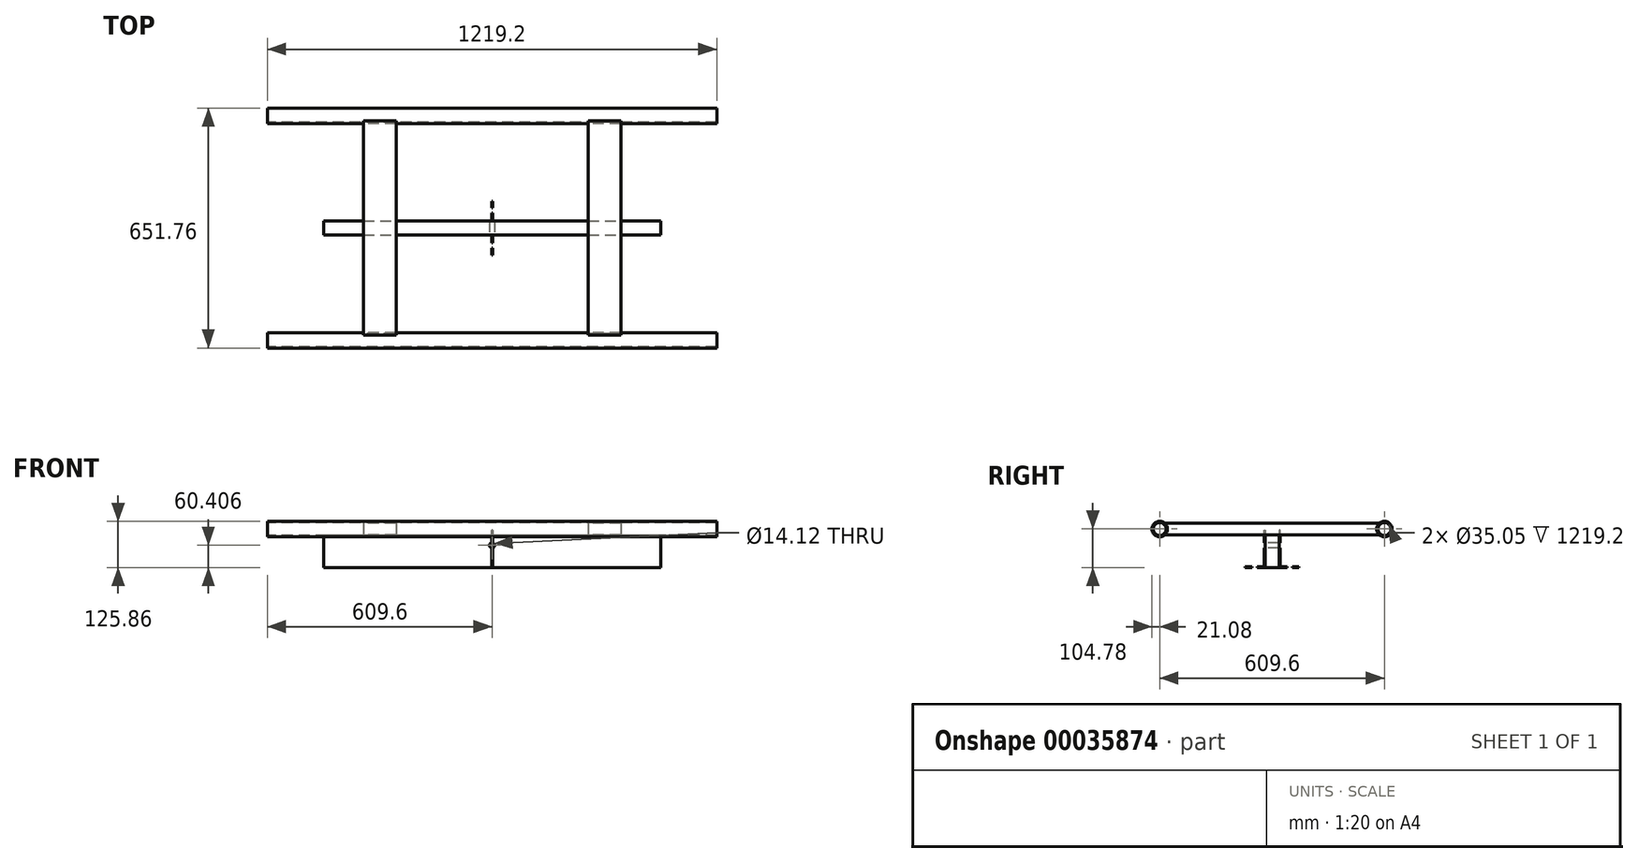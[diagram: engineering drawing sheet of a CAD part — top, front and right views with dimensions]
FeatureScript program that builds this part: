
annotation { "Feature Type Name" : "Feature", "Feature Type Description" : "" }
export const myFeature = defineFeature(function(context is Context, id is Id, definition is map)
    precondition{}
    {
        {
            var Q0;
            Q0=qCreatedBy(makeId("Right.planeOp"),FACE);
            var sketch = newSketch(context, id + "F0", { "sketchPlane" : qUnion([Q0])});
            skCircle(sketch, "E0", {"center": v(-304.8, 0) * mm, "radius": 21.08 * mm});
            skCircle(sketch, "E1", {"center": v(304.8, 0) * mm, "radius": 21.08 * mm});
            skLineSegment(sketch, "E2", {"start": v(-283.72, 0) * mm, "end": v(283.72, 0) * mm, "construction": true});
            skCircle(sketch, "E3", {"center": v(-304.8, 0) * mm, "radius": 17.53 * mm});
            skCircle(sketch, "E4", {"center": v(304.8, 0) * mm, "radius": 17.53 * mm});
            skPoint(sketch, "E5.rect.middle", {"position": v(0, 0) * mm});
            skSolve(sketch);
        }
        {
            var Q0;
            Q0=makeQuery(id+"F0.imprint","IMPRINT",FACE,{"disambiguationData":[TD([[makeQuery(id+"F0.imprint","IMPRINT",EDGE,{"derivedFrom":sQuery(id+"F0.wireOp",EDGE,"E0")}),1.0]])]});
            var Q1;
            Q1=makeQuery(id+"F0.imprint","IMPRINT",FACE,{"disambiguationData":[TD([[makeQuery(id+"F0.imprint","IMPRINT",EDGE,{"derivedFrom":sQuery(id+"F0.wireOp",EDGE,"E1")}),1.0]])]});
            extrude(context, id + "F1", {"entities" : qUnion([Q0, Q1]), "endBound" : BoundingType.SYMMETRIC, "depth" : 1219.2 * mm});
        }
        {
            var Q0;
            Q0=qCreatedBy(makeId("Front.planeOp"),FACE);
            var sketch = newSketch(context, id + "F2", { "sketchPlane" : qUnion([Q0])});
            skLineSegment(sketch, "E6", {"start": v(-304.8, 0) * mm, "end": v(304.8, 0) * mm, "construction": true});
            skLineSegment(sketch, "E7.rect.bottom", {"start": v(-260.35, -15.87) * mm, "end": v(-349.25, -15.87) * mm});
            skLineSegment(sketch, "E7.rect.top", {"start": v(-260.35, 15.88) * mm, "end": v(-349.25, 15.88) * mm});
            skLineSegment(sketch, "E7.rect.left", {"start": v(-260.35, -15.87) * mm, "end": v(-260.35, 15.88) * mm});
            skLineSegment(sketch, "E7.rect.right", {"start": v(-349.25, -15.87) * mm, "end": v(-349.25, 15.88) * mm});
            skPoint(sketch, "E7.rect.middle", {"position": v(-304.8, 0) * mm});
            skLineSegment(sketch, "E8.rect.bottom", {"start": v(349.25, -15.87) * mm, "end": v(260.35, -15.88) * mm});
            skLineSegment(sketch, "E8.rect.top", {"start": v(349.25, 15.88) * mm, "end": v(260.35, 15.88) * mm});
            skLineSegment(sketch, "E8.rect.left", {"start": v(349.25, -15.87) * mm, "end": v(349.25, 15.88) * mm});
            skLineSegment(sketch, "E8.rect.right", {"start": v(260.35, -15.88) * mm, "end": v(260.35, 15.88) * mm});
            skPoint(sketch, "E8.rect.middle", {"position": v(304.8, 0) * mm});
            skSolve(sketch);
        }
        {
            var Q0;
            Q0=makeQuery(id+"F2.imprint","IMPRINT",FACE,{"disambiguationData":[TD([[makeQuery(id+"F2.imprint","IMPRINT",EDGE,{"derivedFrom":sQuery(id+"F2.wireOp",EDGE,"E7.rect.bottom")}),-1.0]])]});
            var Q1;
            Q1=makeQuery(id+"F2.imprint","IMPRINT",FACE,{"disambiguationData":[TD([[makeQuery(id+"F2.imprint","IMPRINT",EDGE,{"derivedFrom":sQuery(id+"F2.wireOp",EDGE,"E8.rect.bottom")}),-1.0]])]});
            extrude(context, id + "F3", {"entities" : qUnion([Q0, Q1]), "endBound" : BoundingType.UP_TO_NEXT, "depth" : 25.4 * mm, "hasSecondDirection" : true, "secondDirectionBound" : SecondDirectionBoundingType.UP_TO_NEXT, "secondDirectionOppositeDirection" : true, "secondDirectionDepth" : 25.4 * mm});
        }
        {
            assignVariable(context, id + "F4", {"name" : "bcLength", "anyValue" : 914.4 * mm});
        }
        {
            var Q0;
            Q0=qCreatedBy(makeId("Right.planeOp"),FACE);
            var sketch = newSketch(context, id + "F5", { "sketchPlane" : qUnion([Q0])});
            skLineSegment(sketch, "E9.bottom", {"start": v(-19.05, -15.88) * mm, "end": v(19.05, -15.88) * mm});
            skLineSegment(sketch, "E9.top", {"start": v(-19.05, -104.78) * mm, "end": v(19.05, -104.78) * mm});
            skLineSegment(sketch, "E9.left", {"start": v(-19.05, -104.78) * mm, "end": v(-19.05, -15.88) * mm});
            skLineSegment(sketch, "E9.right", {"start": v(19.05, -104.78) * mm, "end": v(19.05, -15.87) * mm});
            skPoint(sketch, "E10", {"position": v(0, -15.88) * mm});
            skPoint(sketch, "E11", {"position": v(0, -104.78) * mm});
            skLineSegment(sketch, "E12", {"start": v(0, -104.78) * mm, "end": v(0, -15.88) * mm, "construction": true});
            skSolve(sketch);
        }
        {
            var Q0;
            Q0 = qSketchRegion(id + "F5", true);
            extrude(context, id + "F6", {"entities" : qUnion([Q0]), "endBound" : BoundingType.SYMMETRIC, "oppositeDirection" : true, "depth" : getVariable(context, 'bcLength')});
        }
        {
            assignVariable(context, id + "F7", {"name" : "joistwidth", "anyValue" : 2.5});
        }
        {
            var Q0;
            Q0=qCreatedBy(makeId("Right.planeOp"),FACE);
            var sketch = newSketch(context, id + "F8", { "sketchPlane" : qUnion([Q0])});
            skLineSegment(sketch, "E13", {"start": v(19.05, -3.17) * mm, "end": v(19.05, -104.78) * mm});
            skLineSegment(sketch, "E14", {"start": v(19.05, -104.78) * mm, "end": v(73.03, -104.78) * mm});
            skLineSegment(sketch, "E15", {"start": v(73.03, -104.78) * mm, "end": v(73.03, -102.02) * mm});
            skLineSegment(sketch, "E16", {"start": v(73.03, -102.02) * mm, "end": v(21.8, -102.02) * mm});
            skLineSegment(sketch, "E17", {"start": v(21.8, -102.02) * mm, "end": v(21.8, -3.17) * mm});
            skLineSegment(sketch, "E18", {"start": v(21.8, -3.17) * mm, "end": v(19.05, -3.17) * mm});
            skLineSegment(sketch, "E19", {"start": v(0, 58.44) * mm, "end": v(0, -123.14) * mm, "construction": true});
            skLineSegment(sketch, "E20.MirrorCS", {"start": v(-21.8, -3.17) * mm, "end": v(-19.05, -3.17) * mm});
            skLineSegment(sketch, "E21.MirrorCS", {"start": v(-73.03, -104.78) * mm, "end": v(-73.03, -102.02) * mm});
            skLineSegment(sketch, "E22.MirrorCS", {"start": v(-19.05, -104.78) * mm, "end": v(-73.03, -104.78) * mm});
            skLineSegment(sketch, "E23.MirrorCS", {"start": v(-21.8, -102.02) * mm, "end": v(-21.8, -3.17) * mm});
            skLineSegment(sketch, "E24.MirrorCS", {"start": v(-73.03, -102.02) * mm, "end": v(-21.8, -102.02) * mm});
            skLineSegment(sketch, "E25.MirrorCS", {"start": v(-19.05, -3.17) * mm, "end": v(-19.05, -104.78) * mm});
            skSolve(sketch);
        }
        {
            assignVariable(context, id + "F9", {"name" : "joistwidth", "anyValue" : 2.5});
        }
        {
            var Q0;
            Q0 = qSketchRegion(id + "F8", true);
            extrude(context, id + "F10", {"entities" : qUnion([Q0]), "endBound" : BoundingType.SYMMETRIC, "depth" : (getVariable(context, 'joistwidth')) * mm});
        }
        {
            var Q0;
            Q0=makeQuery(id+"F10.opExtrude","SWEPT_EDGE",EDGE,{"disambiguationData":[OSD([sQuery(id+"F8.wireOp",EDGE,"E16"),sQuery(id+"F8.wireOp",EDGE,"E17")])]});
            var Q1;
            Q1=makeQuery(id+"F10.opExtrude","SWEPT_EDGE",EDGE,{"disambiguationData":[OSD([sQuery(id+"F8.wireOp",EDGE,"E13"),sQuery(id+"F8.wireOp",EDGE,"E14")])]});
            var Q2;
            Q2=makeQuery(id+"F10.opExtrude","SWEPT_EDGE",EDGE,{"disambiguationData":[OSD([sQuery(id+"F8.wireOp",EDGE,"E22.MirrorCS"),sQuery(id+"F8.wireOp",EDGE,"E25.MirrorCS")])]});
            var Q3;
            Q3=makeQuery(id+"F10.opExtrude","SWEPT_EDGE",EDGE,{"disambiguationData":[OSD([sQuery(id+"F8.wireOp",EDGE,"E23.MirrorCS"),sQuery(id+"F8.wireOp",EDGE,"E24.MirrorCS")])]});
            fillet(context, id + "F11", {"entities" : qUnion([Q0, Q1, Q2, Q3]), "radius" : 2.54 * mm, "tangentPropagation" : true, "allowEdgeOverflow" : false});
        }
        {
            var Q0;
            Q0=qCreatedBy(makeId("Front.planeOp"),FACE);
            var sketch = newSketch(context, id + "F12", { "sketchPlane" : qUnion([Q0])});
            skCircle(sketch, "E26", {"center": v(0, -44.37) * mm, "radius": 7.06 * mm});
            skSolve(sketch);
        }
        {
            var Q0;
            Q0 = qSketchRegion(id + "F12", true);
            extrude(context, id + "F13", {"entities" : qUnion([Q0]), "operationType" : NewBodyOperationType.REMOVE, "endBound" : BoundingType.SYMMETRIC, "oppositeDirection" : true, "depth" : 101.6 * mm, "hasSecondDirection" : true, "secondDirectionOppositeDirection" : false, "secondDirectionDepth" : 25.4 * mm});
        }
        {
            var Q0;
            Q0=makeQuery(id+"F10.opExtrude","SWEPT_FACE",FACE,{"disambiguationData":[OSD([sQuery(id+"F8.wireOp",EDGE,"E24.MirrorCS")])]});
            var sketch = newSketch(context, id + "F14", { "sketchPlane" : qUnion([Q0])});
            skCircle(sketch, "E27", {"center": v(0, -47.62) * mm, "radius": 7.06 * mm});
            skCircle(sketch, "E28.MirrorC", {"center": v(0, 47.63) * mm, "radius": 7.06 * mm});
            skSolve(sketch);
        }
        {
            var Q0;
            Q0 = qSketchRegion(id + "F14", true);
            extrude(context, id + "F15", {"entities" : qUnion([Q0]), "operationType" : NewBodyOperationType.REMOVE, "endBound" : BoundingType.UP_TO_NEXT, "oppositeDirection" : true, "depth" : 25.4 * mm});
        }
    });
